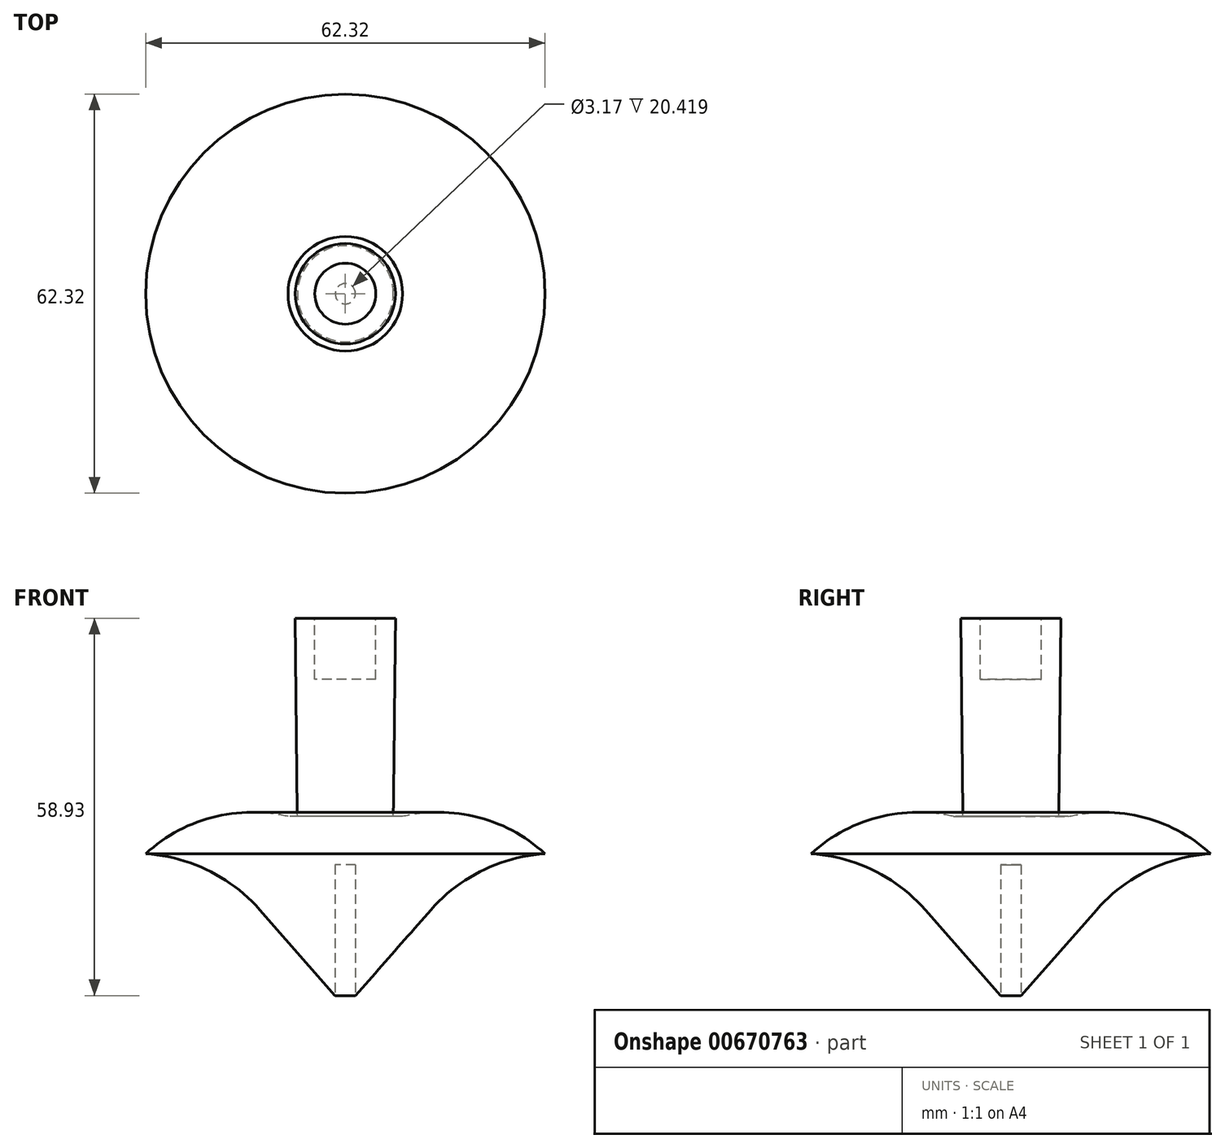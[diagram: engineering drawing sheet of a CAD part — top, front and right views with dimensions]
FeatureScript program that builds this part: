
annotation { "Feature Type Name" : "Feature", "Feature Type Description" : "" }
export const myFeature = defineFeature(function(context is Context, id is Id, definition is map)
    precondition{}
    {
        {
            var Q0;
            Q0=qCreatedBy(makeId("Front.planeOp"),FACE);
            var sketch = newSketch(context, id + "F0", { "sketchPlane" : qUnion([Q0])});
            skLineSegment(sketch, "E0", {"start": v(0, 0) * mm, "end": v(13.37, 15.2) * mm});
            skArc(sketch, "E1", {"start": v(13.37, 15.2) * mm, "mid": v(21.4, 21.35) * mm, "end": v(31.16, 23.96) * mm});
            skArc(sketch, "E2", {"start": v(31.16, 23.96) * mm, "mid": v(20.78, 29.64) * mm, "end": v(8.94, 29.77) * mm});
            skLineSegment(sketch, "E3", {"start": v(8.94, 29.77) * mm, "end": v(7.49, 29.77) * mm});
            skLineSegment(sketch, "E4", {"start": v(7.84, 60.74) * mm, "end": v(0, 60.74) * mm});
            skLineSegment(sketch, "E5", {"start": v(0, 60.74) * mm, "end": v(0, 0) * mm});
            skLineSegment(sketch, "E6", {"start": v(7.84, 60.74) * mm, "end": v(7.49, 29.77) * mm});
            skSolve(sketch);
        }
        {
            var Q0;
            Q0 = qSketchRegion(id + "F0", true);
            var Q1;
            Q1=sQuery(id+"F0.wireOp",EDGE,"E5");
            revolve(context, id + "F1", {"entities" : qUnion([Q0]), "axis" : qUnion([Q1]), "revolveType" : RevolveType.FULL, "surfaceOperationType" : NewSurfaceOperationType.NEW});
        }
        {
            var Q0;
            Q0=makeQuery(id+"F1.opRevolve","SWEPT_FACE",FACE,{"disambiguationData":[OSD([sQuery(id+"F0.wireOp",EDGE,"E4")])]});
            var sketch = newSketch(context, id + "F2", { "sketchPlane" : qUnion([Q0])});
            skCircle(sketch, "E7", {"center": v(0, 0) * mm, "radius": 4.76 * mm});
            skSolve(sketch);
        }
        {
            var Q0;
            Q0 = qSketchRegion(id + "F2", true);
            extrude(context, id + "F3", {"entities" : qUnion([Q0]), "operationType" : NewBodyOperationType.REMOVE, "oppositeDirection" : true, "depth" : 9.52 * mm, "offsetDistance" : 25.4 * mm});
        }
        {
            var Q0;
            Q0=qCreatedBy(makeId("Top.planeOp"),FACE);
            var sketch = newSketch(context, id + "F4", { "sketchPlane" : qUnion([Q0])});
            skCircle(sketch, "E8", {"center": v(0, 0) * mm, "radius": 1.59 * mm});
            skSolve(sketch);
        }
        {
            var Q0;
            Q0=makeQuery(id+"F4.imprint","IMPRINT",FACE,{"disambiguationData":[TD([[makeQuery(id+"F4.imprint","IMPRINT",EDGE,{"derivedFrom":sQuery(id+"F4.wireOp",EDGE,"E8")}),1.0]])]});
            extrude(context, id + "F5", {"entities" : qUnion([Q0]), "operationType" : NewBodyOperationType.REMOVE, "depth" : 22.22 * mm, "offsetDistance" : 25.4 * mm});
        }
    });
